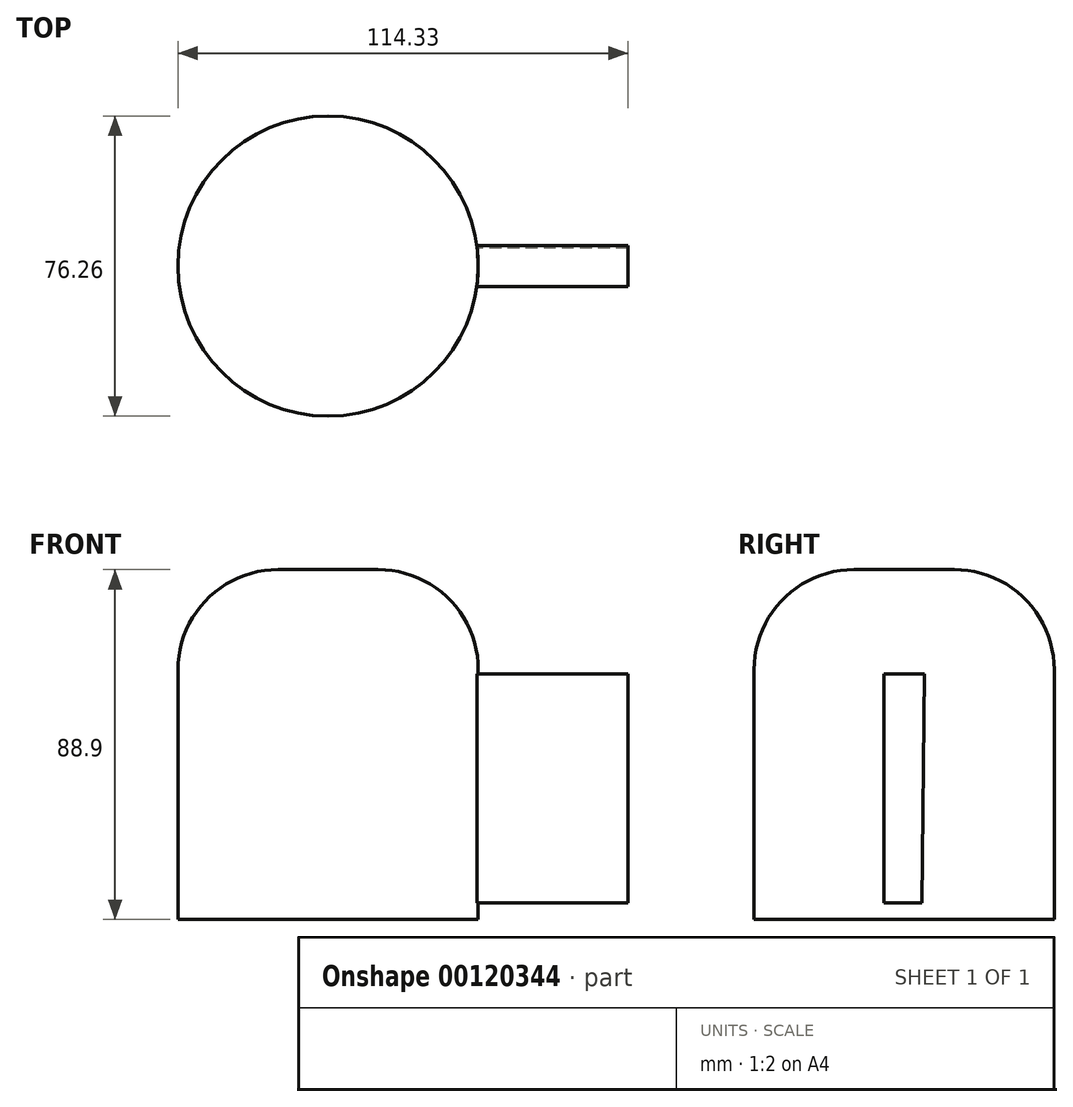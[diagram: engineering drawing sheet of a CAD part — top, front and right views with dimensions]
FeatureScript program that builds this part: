
annotation { "Feature Type Name" : "Feature", "Feature Type Description" : "" }
export const myFeature = defineFeature(function(context is Context, id is Id, definition is map)
    precondition{}
    {
        {
            var Q0;
            Q0=qCreatedBy(makeId("Top.planeOp"),FACE);
            var sketch = newSketch(context, id + "F0", { "sketchPlane" : qUnion([Q0])});
            skCircle(sketch, "E0", {"center": v(0, 0) * mm, "radius": 38.13 * mm});
            skSolve(sketch);
        }
        {
            var Q0;
            Q0=makeQuery(id+"F0.imprint","IMPRINT",FACE,{"disambiguationData":[TD([[makeQuery(id+"F0.imprint","IMPRINT",EDGE,{"derivedFrom":sQuery(id+"F0.wireOp",EDGE,"E0")}),1.0]])]});
            extrude(context, id + "F1", {"entities" : qUnion([Q0]), "depth" : 88.9 * mm});
        }
        {
            var Q0;
            Q0=makeQuery(id+"F1.opExtrude","CAP_EDGE",EDGE,{"disambiguationData":[OSD([sQuery(id+"F0.wireOp",EDGE,"E0")])],"isStart":false});
            fillet(context, id + "F2", {"entities" : qUnion([Q0]), "radius" : 25.4 * mm, "tangentPropagation" : true, "allowEdgeOverflow" : false});
        }
        {
            var Q0;
            Q0=qCreatedBy(makeId("Right.planeOp"),FACE);
            var sketch = newSketch(context, id + "F3", { "sketchPlane" : qUnion([Q0])});
            skLineSegment(sketch, "E1", {"start": v(5.17, 62.36) * mm, "end": v(-5.17, 62.36) * mm});
            skLineSegment(sketch, "E2", {"start": v(-5.17, 62.36) * mm, "end": v(-5.17, 4.25) * mm});
            skLineSegment(sketch, "E3", {"start": v(-5.17, 4.25) * mm, "end": v(4.52, 4.25) * mm});
            skLineSegment(sketch, "E4", {"start": v(4.52, 4.25) * mm, "end": v(5.17, 62.36) * mm});
            skSolve(sketch);
        }
        {
            var Q0;
            Q0 = qSketchRegion(id + "F3", true);
            extrude(context, id + "F4", {"entities" : qUnion([Q0]), "operationType" : NewBodyOperationType.ADD, "depth" : 76.2 * mm});
        }
    });
